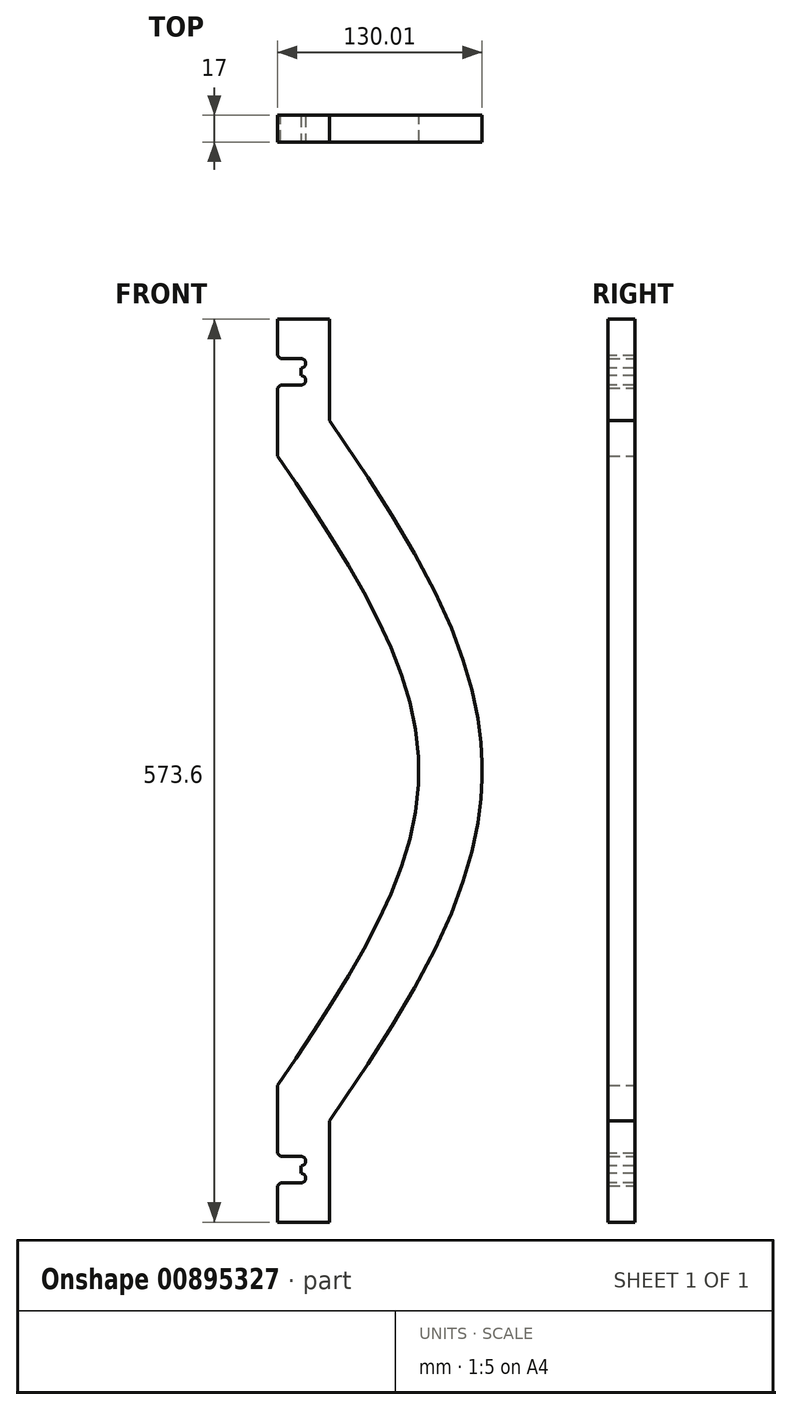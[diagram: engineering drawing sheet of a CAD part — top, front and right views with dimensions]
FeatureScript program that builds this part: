
annotation { "Feature Type Name" : "Feature", "Feature Type Description" : "" }
export const myFeature = defineFeature(function(context is Context, id is Id, definition is map)
    precondition{}
    {
        {
            var Q0;
            Q0=qCreatedBy(makeId("Front.planeOp"),FACE);
            var sketch = newSketch(context, id + "F0", { "sketchPlane" : qUnion([Q0])});
            skLineSegment(sketch, "E0", {"start": v(0, 200) * mm, "end": v(0, -200) * mm, "construction": true});
            skLineSegment(sketch, "E1", {"start": v(0, 0) * mm, "end": v(90, 0) * mm, "construction": true});
            skFitSpline(sketch, "E2", {"points": [v(0, 200) * mm, v(90, 0) * mm, v(0, -200) * mm], "startDerivative": vector(270, -400) * mm, "endDerivative": vector(-270, -400) * mm});
            skFitSpline(sketch, "E3.0", {"points": [v(33.15, 222.38) * mm, v(38.78, 214.05) * mm, v(50.14, 197.22) * mm, v(66.97, 171.48) * mm, v(83.07, 145.18) * mm, v(97.88, 118.2) * mm, v(108.65, 95.03) * mm, v(116, 75.96) * mm, v(120.77, 61.38) * mm, v(124.7, 46.5) * mm, v(127.17, 33.83) * mm, v(128.61, 23.55) * mm, v(129.4, 15.77) * mm, v(129.8, 9.23) * mm, v(129.97, 3.96) * mm, v(130.01, 0) * mm, v(129.97, -3.96) * mm, v(129.8, -9.23) * mm, v(129.4, -15.77) * mm, v(128.61, -23.55) * mm, v(127.17, -33.83) * mm, v(124.7, -46.5) * mm, v(120.77, -61.38) * mm, v(116, -75.96) * mm, v(108.65, -95.03) * mm, v(97.88, -118.2) * mm, v(83.07, -145.18) * mm, v(66.97, -171.48) * mm, v(50.14, -197.22) * mm, v(38.78, -214.05) * mm, v(33.15, -222.38) * mm]});
            skLineSegment(sketch, "E4", {"start": v(33.15, 222.38) * mm, "end": v(33.15, 286.8) * mm});
            skLineSegment(sketch, "E5", {"start": v(33.15, 286.8) * mm, "end": v(0, 286.8) * mm});
            skLineSegment(sketch, "E6", {"start": v(0, 286.8) * mm, "end": v(0, 261.8) * mm});
            skLineSegment(sketch, "E7", {"start": v(0, 261.8) * mm, "end": v(15, 261.8) * mm});
            skLineSegment(sketch, "E8", {"start": v(15, 261.8) * mm, "end": v(15, 245) * mm});
            skLineSegment(sketch, "E9", {"start": v(15, 245) * mm, "end": v(0, 245) * mm});
            skLineSegment(sketch, "E10", {"start": v(0, 245) * mm, "end": v(0, 200) * mm});
            skLineSegment(sketch, "E11.MirrorCS", {"start": v(15, -245) * mm, "end": v(0, -245) * mm});
            skLineSegment(sketch, "E12.MirrorCS", {"start": v(15, -261.8) * mm, "end": v(15, -245) * mm});
            skLineSegment(sketch, "E13.MirrorCS", {"start": v(0, -286.8) * mm, "end": v(0, -261.8) * mm});
            skLineSegment(sketch, "E14.MirrorCS", {"start": v(33.15, -222.38) * mm, "end": v(33.15, -286.8) * mm});
            skLineSegment(sketch, "E15.MirrorCS", {"start": v(33.15, -286.8) * mm, "end": v(0, -286.8) * mm});
            skLineSegment(sketch, "E16.MirrorCS", {"start": v(0, -245) * mm, "end": v(0, -200) * mm});
            skLineSegment(sketch, "E17.MirrorCS", {"start": v(0, -261.8) * mm, "end": v(15, -261.8) * mm});
            skSolve(sketch);
        }
        {
            var Q0;
            Q0=makeQuery(id+"F0.imprint","IMPRINT",FACE,{"disambiguationData":[TD([[makeQuery(id+"F0.imprint","IMPRINT",EDGE,{"derivedFrom":sQuery(id+"F0.wireOp",EDGE,"E2")}),1.0]])]});
            extrude(context, id + "F1", {"entities" : qUnion([Q0]), "depth" : 17 * mm, "offsetDistance" : 25 * mm});
        }
        {
            var Q0;
            Q0=makeQuery(id+"F1.opExtrude","CAP_FACE",FACE,{"disambiguationData":[OSD([sQuery(id+"F0.wireOp",EDGE,"E2"),sQuery(id+"F0.wireOp",EDGE,"E3.0"),sQuery(id+"F0.wireOp",EDGE,"E4"),sQuery(id+"F0.wireOp",EDGE,"E5"),sQuery(id+"F0.wireOp",EDGE,"E6"),sQuery(id+"F0.wireOp",EDGE,"E7"),sQuery(id+"F0.wireOp",EDGE,"E8"),sQuery(id+"F0.wireOp",EDGE,"E9"),sQuery(id+"F0.wireOp",EDGE,"E10"),sQuery(id+"F0.wireOp",EDGE,"E12.MirrorCS"),sQuery(id+"F0.wireOp",EDGE,"E13.MirrorCS"),sQuery(id+"F0.wireOp",EDGE,"E14.MirrorCS"),sQuery(id+"F0.wireOp",EDGE,"E15.MirrorCS"),sQuery(id+"F0.wireOp",EDGE,"E16.MirrorCS"),sQuery(id+"F0.wireOp",EDGE,"E17.MirrorCS"),sQuery(id+"F0.wireOp",EDGE,"E11.MirrorCS")])],"isStart":false});
            var sketch = newSketch(context, id + "F2", { "sketchPlane" : qUnion([Q0])});
            skCircle(sketch, "E18", {"center": v(15, 248) * mm, "radius": 3 * mm});
            skLineSegment(sketch, "E19", {"start": v(15, 253.4) * mm, "end": v(9.17, 253.4) * mm, "construction": true});
            skCircle(sketch, "E20.MirrorC", {"center": v(15, 258.8) * mm, "radius": 3 * mm});
            skCircle(sketch, "E21.MirrorC", {"center": v(15, -248) * mm, "radius": 3 * mm});
            skCircle(sketch, "E22.MirrorC", {"center": v(15, -258.8) * mm, "radius": 3 * mm});
            skSolve(sketch);
        }
        {
            var Q0;
            Q0 = qSketchRegion(id + "F2", true);
            extrude(context, id + "F3", {"entities" : qUnion([Q0]), "operationType" : NewBodyOperationType.REMOVE, "oppositeDirection" : true, "depth" : 25 * mm, "offsetDistance" : 25 * mm});
        }
        {
            var Q0;
            Q0=makeQuery(id+"F1.opExtrude","SWEPT_EDGE",EDGE,{"disambiguationData":[OSD([sQuery(id+"F0.wireOp",EDGE,"E6"),sQuery(id+"F0.wireOp",EDGE,"E7")])]});
            var Q1;
            Q1=makeQuery(id+"F1.opExtrude","SWEPT_EDGE",EDGE,{"disambiguationData":[OSD([sQuery(id+"F0.wireOp",EDGE,"E9"),sQuery(id+"F0.wireOp",EDGE,"E10")])]});
            var Q2;
            Q2=makeQuery(id+"F1.opExtrude","SWEPT_EDGE",EDGE,{"disambiguationData":[OSD([sQuery(id+"F0.wireOp",EDGE,"E16.MirrorCS"),sQuery(id+"F0.wireOp",EDGE,"E11.MirrorCS")])]});
            var Q3;
            Q3=makeQuery(id+"F1.opExtrude","SWEPT_EDGE",EDGE,{"disambiguationData":[OSD([sQuery(id+"F0.wireOp",EDGE,"E13.MirrorCS"),sQuery(id+"F0.wireOp",EDGE,"E17.MirrorCS")])]});
            chamfer(context, id + "F4", {"entities" : qUnion([Q0, Q1, Q2, Q3]), "width" : 2 * mm, "tangentPropagation" : true});
        }
    });
